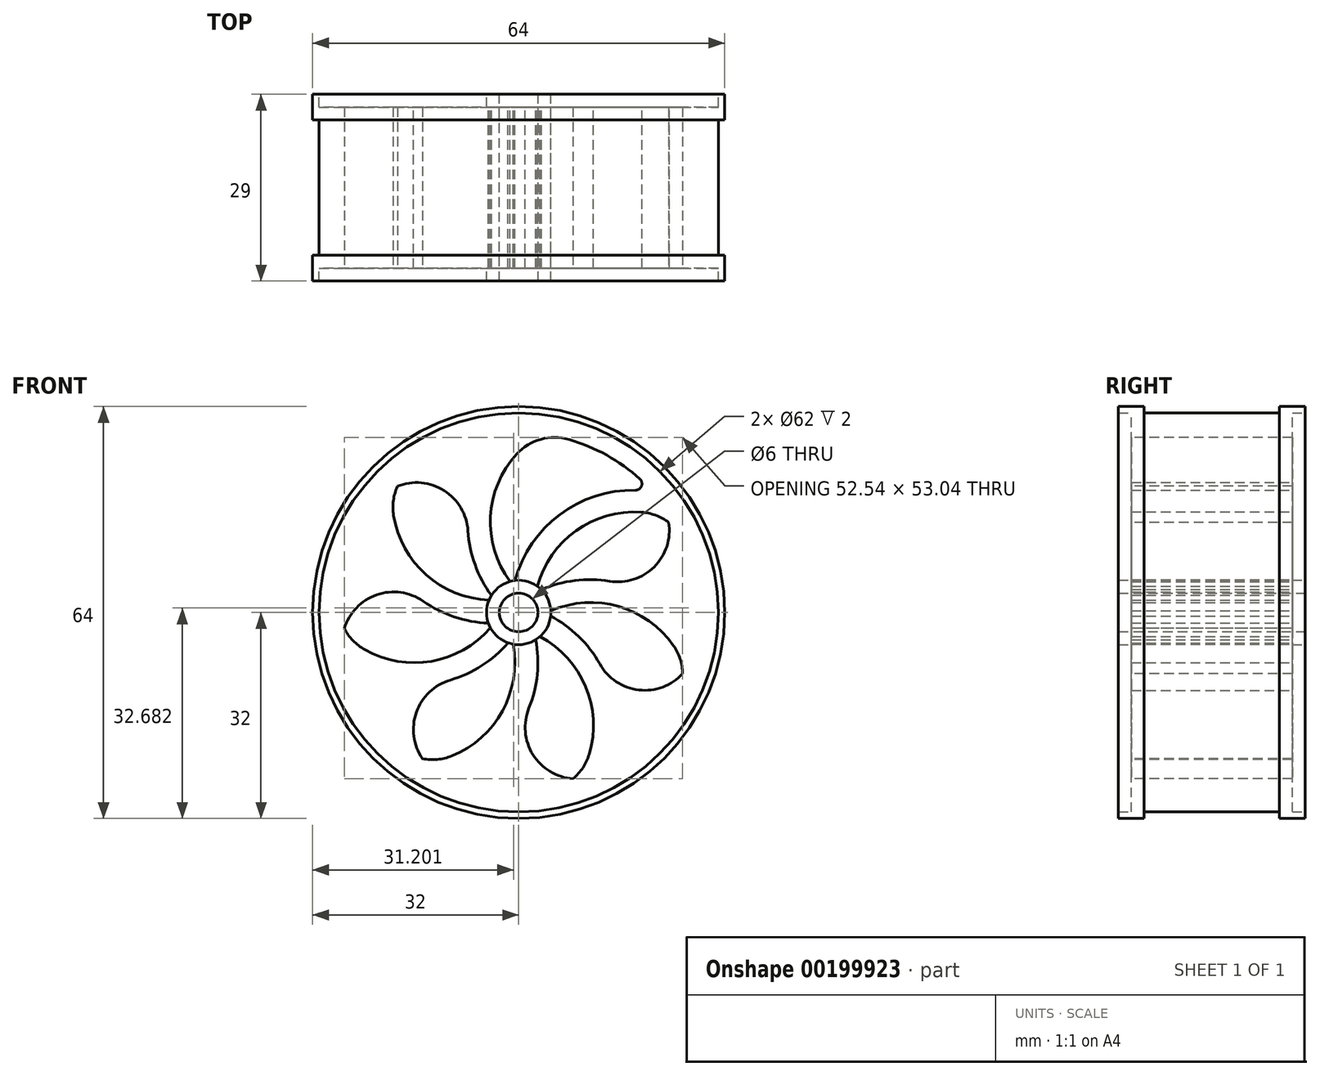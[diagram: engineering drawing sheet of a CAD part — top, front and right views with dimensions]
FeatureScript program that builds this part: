
annotation { "Feature Type Name" : "Feature", "Feature Type Description" : "" }
export const myFeature = defineFeature(function(context is Context, id is Id, definition is map)
    precondition{}
    {
        {
            var Q0;
            Q0=qCreatedBy(makeId("Front.planeOp"),FACE);
            var sketch = newSketch(context, id + "F0", { "sketchPlane" : qUnion([Q0])});
            skCircle(sketch, "E0", {"center": v(0, 0) * mm, "radius": 3 * mm});
            skCircle(sketch, "E1", {"center": v(0, 0) * mm, "radius": 5 * mm});
            skCircle(sketch, "E2", {"center": v(0, 0) * mm, "radius": 28 * mm});
            skCircle(sketch, "E3", {"center": v(0, 0) * mm, "radius": 31 * mm});
            skCircle(sketch, "E4", {"center": v(0, 0) * mm, "radius": 32 * mm});
            skArc(sketch, "E5", {"start": v(23.84, 14.68) * mm, "mid": v(11.32, 13.16) * mm, "end": v(4.15, 2.79) * mm, "construction": true});
            skArc(sketch, "E6", {"start": v(20.79, 18.76) * mm, "mid": v(7.46, 15.96) * mm, "end": v(-0.56, 4.97) * mm});
            skArc(sketch, "E7.trimOffspring", {"start": v(24, 14.41) * mm, "mid": v(11.11, 14.02) * mm, "end": v(2.92, 4.06) * mm});
            skPoint(sketch, "E8.center.orphan", {"position": v(20.77, 0) * mm});
            skSolve(sketch);
        }
        {
            var Q0;
            Q0=makeQuery(id+"F0.imprint","IMPRINT",FACE,{"disambiguationData":[TD([[makeQuery(id+"F0.imprint","IMPRINT",EDGE,{"derivedFrom":sQuery(id+"F0.wireOp",EDGE,"E3")}),1.0]])]});
            var Q1;
            {var subQ0=sQuery(id+"F0.wireOp",EDGE,"E6");Q1=makeQuery(id+"F0.imprint","IMPRINT",FACE,{"disambiguationData":[TD([[makeQuery(id+"F0.imprint","IMPRINT",EDGE,{"derivedFrom":subQ0}),1.0]])]});}
            var Q2;
            Q2=makeQuery(id+"F0.imprint","IMPRINT",FACE,{"disambiguationData":[TD([[makeQuery(id+"F0.imprint","IMPRINT",EDGE,{"derivedFrom":sQuery(id+"F0.wireOp",EDGE,"E0")}),-1.0]])]});
            extrude(context, id + "F1", {"entities" : qUnion([Q0, Q1, Q2]), "depth" : 25 * mm});
        }
        {
            var Q0;
            Q0=makeQuery(id+"F1.opExtrude","SWEPT_BODY",BODY,{"disambiguationData":[OSD([sQuery(id+"F0.wireOp",EDGE,"E0"),sQuery(id+"F0.wireOp",EDGE,"E1"),sQuery(id+"F0.wireOp",EDGE,"E2"),sQuery(id+"F0.wireOp",EDGE,"E3"),sQuery(id+"F0.wireOp",EDGE,"E6"),sQuery(id+"F0.wireOp",EDGE,"E7.trimOffspring")])]});
            var Q1;
            Q1=makeQuery(id+"F1.opExtrude","CAP_EDGE",EDGE,{"disambiguationData":[OSD([sQuery(id+"F0.wireOp",EDGE,"E0")])],"isStart":true});
            circularPattern(context, id + "F2", {"entities" : qUnion([Q0]), "axis" : qUnion([Q1]), "angle" : 360 * degree, "instanceCount" : 7, "equalSpace" : true});
        }
        {
            var Q0;
            Q0=makeQuery(id+"F0.imprint","IMPRINT",FACE,{"disambiguationData":[TD([[makeQuery(id+"F0.imprint","IMPRINT",EDGE,{"derivedFrom":sQuery(id+"F0.wireOp",EDGE,"E0")}),-1.0]])]});
            extrude(context, id + "F3", {"entities" : qUnion([Q0]), "operationType" : NewBodyOperationType.ADD, "depth" : 27 * mm});
        }
        {
            var Q0;
            Q0=makeQuery(id+"F0.imprint","IMPRINT",FACE,{"disambiguationData":[TD([[makeQuery(id+"F0.imprint","IMPRINT",EDGE,{"derivedFrom":sQuery(id+"F0.wireOp",EDGE,"E0")}),-1.0]])]});
            extrude(context, id + "F4", {"entities" : qUnion([Q0]), "operationType" : NewBodyOperationType.ADD, "oppositeDirection" : true, "depth" : 2 * mm});
        }
        {
            var Q0;
            Q0=makeQuery(id+"F0.imprint","IMPRINT",FACE,{"disambiguationData":[TD([[makeQuery(id+"F0.imprint","IMPRINT",EDGE,{"derivedFrom":sQuery(id+"F0.wireOp",EDGE,"E3")}),-1.0]])]});
            extrude(context, id + "F5", {"entities" : qUnion([Q0]), "operationType" : NewBodyOperationType.ADD, "depth" : 27 * mm});
        }
        {
            var Q0;
            Q0=makeQuery(id+"F0.imprint","IMPRINT",FACE,{"disambiguationData":[TD([[makeQuery(id+"F0.imprint","IMPRINT",EDGE,{"derivedFrom":sQuery(id+"F0.wireOp",EDGE,"E3")}),-1.0]])]});
            extrude(context, id + "F6", {"entities" : qUnion([Q0]), "operationType" : NewBodyOperationType.REMOVE, "depth" : 23 * mm});
        }
        {
            var Q0;
            Q0=makeQuery(id+"F0.imprint","IMPRINT",FACE,{"disambiguationData":[TD([[makeQuery(id+"F0.imprint","IMPRINT",EDGE,{"derivedFrom":sQuery(id+"F0.wireOp",EDGE,"E3")}),-1.0]])]});
            extrude(context, id + "F7", {"entities" : qUnion([Q0]), "operationType" : NewBodyOperationType.ADD, "endBound" : BoundingType.SYMMETRIC, "depth" : 4 * mm});
        }
        {
            var Q0;
            {var subQ0=makeQuery(id+"F1.opExtrude","SWEPT_FACE",FACE,{"disambiguationData":[OSD([sQuery(id+"F0.wireOp",EDGE,"E2")])]});Q0=makeQuery(id+"F3.boolean.opBoolean","INTERSECT",EDGE,{"disambiguationData":[OD(1.0)],"derivedFrom":[subQ0,makeQuery(id+"F2.opPattern","COPY",FACE,{"derivedFrom":subQ0,"instanceName":"1"}),makeQuery(id+"F2.opPattern","COPY",FACE,{"derivedFrom":subQ0,"instanceName":"2"}),makeQuery(id+"F2.opPattern","COPY",FACE,{"derivedFrom":subQ0,"instanceName":"4"})]});}
            var Q1;
            {var subQ0=makeQuery(id+"F1.opExtrude","SWEPT_FACE",FACE,{"disambiguationData":[OSD([sQuery(id+"F0.wireOp",EDGE,"E2")])]});Q1=makeQuery(id+"F3.boolean.opBoolean","INTERSECT",EDGE,{"disambiguationData":[OD(1.0)],"derivedFrom":[subQ0,makeQuery(id+"F2.opPattern","COPY",FACE,{"derivedFrom":subQ0,"instanceName":"1"}),makeQuery(id+"F2.opPattern","COPY",FACE,{"derivedFrom":subQ0,"instanceName":"2"}),makeQuery(id+"F2.opPattern","COPY",FACE,{"derivedFrom":subQ0,"instanceName":"3"}),makeQuery(id+"F2.opPattern","COPY",FACE,{"derivedFrom":subQ0,"instanceName":"5"})]});}
            var Q2;
            {var subQ0=makeQuery(id+"F1.opExtrude","SWEPT_FACE",FACE,{"disambiguationData":[OSD([sQuery(id+"F0.wireOp",EDGE,"E2")])]});Q2=makeQuery(id+"F3.boolean.opBoolean","INTERSECT",EDGE,{"disambiguationData":[OD(1.0)],"derivedFrom":[subQ0,makeQuery(id+"F2.opPattern","COPY",FACE,{"derivedFrom":subQ0,"instanceName":"1"}),makeQuery(id+"F2.opPattern","COPY",FACE,{"derivedFrom":subQ0,"instanceName":"2"}),makeQuery(id+"F2.opPattern","COPY",FACE,{"derivedFrom":subQ0,"instanceName":"3"}),makeQuery(id+"F2.opPattern","COPY",FACE,{"derivedFrom":subQ0,"instanceName":"4"}),makeQuery(id+"F2.opPattern","COPY",FACE,{"derivedFrom":subQ0,"instanceName":"6"})]});}
            var Q3;
            {var subQ0=makeQuery(id+"F1.opExtrude","SWEPT_FACE",FACE,{"disambiguationData":[OSD([sQuery(id+"F0.wireOp",EDGE,"E2")])]});Q3=makeQuery(id+"F3.boolean.opBoolean","INTERSECT",EDGE,{"disambiguationData":[OD(1.0)],"derivedFrom":[subQ0,makeQuery(id+"F2.opPattern","COPY",FACE,{"derivedFrom":subQ0,"instanceName":"1"}),makeQuery(id+"F2.opPattern","COPY",FACE,{"derivedFrom":subQ0,"instanceName":"2"}),makeQuery(id+"F2.opPattern","COPY",FACE,{"derivedFrom":subQ0,"instanceName":"3"}),makeQuery(id+"F2.opPattern","COPY",FACE,{"derivedFrom":subQ0,"instanceName":"4"}),makeQuery(id+"F2.opPattern","COPY",FACE,{"derivedFrom":subQ0,"instanceName":"5"})]});}
            var Q4;
            Q4=makeQuery(id+"F1.opExtrude","SWEPT_EDGE",EDGE,{"disambiguationData":[OSD([sQuery(id+"F0.wireOp",EDGE,"E2"),sQuery(id+"F0.wireOp",EDGE,"E7.trimOffspring")])]});
            var Q5;
            {var subQ0=makeQuery(id+"F1.opExtrude","SWEPT_FACE",FACE,{"disambiguationData":[OSD([sQuery(id+"F0.wireOp",EDGE,"E2")])]});Q5=makeQuery(id+"F3.boolean.opBoolean","INTERSECT",EDGE,{"disambiguationData":[OD(1.0)],"derivedFrom":[subQ0,makeQuery(id+"F2.opPattern","COPY",FACE,{"derivedFrom":subQ0,"instanceName":"2"})]});}
            var Q6;
            {var subQ0=makeQuery(id+"F1.opExtrude","SWEPT_FACE",FACE,{"disambiguationData":[OSD([sQuery(id+"F0.wireOp",EDGE,"E2")])]});Q6=makeQuery(id+"F3.boolean.opBoolean","INTERSECT",EDGE,{"disambiguationData":[OD(1.0)],"derivedFrom":[subQ0,makeQuery(id+"F2.opPattern","COPY",FACE,{"derivedFrom":subQ0,"instanceName":"1"}),makeQuery(id+"F2.opPattern","COPY",FACE,{"derivedFrom":subQ0,"instanceName":"3"})]});}
            fillet(context, id + "F8", {"entities" : qUnion([Q0, Q1, Q2, Q3, Q4, Q5, Q6]), "radius" : 8 * mm, "tangentPropagation" : true, "allowEdgeOverflow" : false});
        }
        {
            var Q0;
            {var subQ0=makeQuery(id+"F1.opExtrude","SWEPT_FACE",FACE,{"disambiguationData":[OSD([sQuery(id+"F0.wireOp",EDGE,"E2")])]});Q0=makeQuery(id+"F3.boolean.opBoolean","INTERSECT",EDGE,{"disambiguationData":[OD(0.0)],"derivedFrom":[subQ0,makeQuery(id+"F2.opPattern","COPY",FACE,{"derivedFrom":subQ0,"instanceName":"1"}),makeQuery(id+"F2.opPattern","COPY",FACE,{"derivedFrom":subQ0,"instanceName":"3"})]});}
            var Q1;
            {var subQ0=makeQuery(id+"F1.opExtrude","SWEPT_FACE",FACE,{"disambiguationData":[OSD([sQuery(id+"F0.wireOp",EDGE,"E2")])]});Q1=makeQuery(id+"F3.boolean.opBoolean","INTERSECT",EDGE,{"disambiguationData":[OD(0.0)],"derivedFrom":[subQ0,makeQuery(id+"F2.opPattern","COPY",FACE,{"derivedFrom":subQ0,"instanceName":"2"})]});}
            var Q2;
            Q2=makeQuery(id+"F1.opExtrude","SWEPT_EDGE",EDGE,{"disambiguationData":[OSD([sQuery(id+"F0.wireOp",EDGE,"E2"),sQuery(id+"F0.wireOp",EDGE,"E6")])]});
            var Q3;
            {var subQ0=makeQuery(id+"F1.opExtrude","SWEPT_FACE",FACE,{"disambiguationData":[OSD([sQuery(id+"F0.wireOp",EDGE,"E2")])]});Q3=makeQuery(id+"F3.boolean.opBoolean","INTERSECT",EDGE,{"disambiguationData":[OD(0.0)],"derivedFrom":[subQ0,makeQuery(id+"F2.opPattern","COPY",FACE,{"derivedFrom":subQ0,"instanceName":"1"}),makeQuery(id+"F2.opPattern","COPY",FACE,{"derivedFrom":subQ0,"instanceName":"2"}),makeQuery(id+"F2.opPattern","COPY",FACE,{"derivedFrom":subQ0,"instanceName":"3"}),makeQuery(id+"F2.opPattern","COPY",FACE,{"derivedFrom":subQ0,"instanceName":"4"}),makeQuery(id+"F2.opPattern","COPY",FACE,{"derivedFrom":subQ0,"instanceName":"5"})]});}
            var Q4;
            {var subQ0=makeQuery(id+"F1.opExtrude","SWEPT_FACE",FACE,{"disambiguationData":[OSD([sQuery(id+"F0.wireOp",EDGE,"E2")])]});Q4=makeQuery(id+"F3.boolean.opBoolean","INTERSECT",EDGE,{"disambiguationData":[OD(0.0)],"derivedFrom":[subQ0,makeQuery(id+"F2.opPattern","COPY",FACE,{"derivedFrom":subQ0,"instanceName":"1"}),makeQuery(id+"F2.opPattern","COPY",FACE,{"derivedFrom":subQ0,"instanceName":"2"}),makeQuery(id+"F2.opPattern","COPY",FACE,{"derivedFrom":subQ0,"instanceName":"3"}),makeQuery(id+"F2.opPattern","COPY",FACE,{"derivedFrom":subQ0,"instanceName":"4"}),makeQuery(id+"F2.opPattern","COPY",FACE,{"derivedFrom":subQ0,"instanceName":"6"})]});}
            var Q5;
            {var subQ0=makeQuery(id+"F1.opExtrude","SWEPT_FACE",FACE,{"disambiguationData":[OSD([sQuery(id+"F0.wireOp",EDGE,"E2")])]});Q5=makeQuery(id+"F3.boolean.opBoolean","INTERSECT",EDGE,{"disambiguationData":[OD(0.0)],"derivedFrom":[subQ0,makeQuery(id+"F2.opPattern","COPY",FACE,{"derivedFrom":subQ0,"instanceName":"1"}),makeQuery(id+"F2.opPattern","COPY",FACE,{"derivedFrom":subQ0,"instanceName":"2"}),makeQuery(id+"F2.opPattern","COPY",FACE,{"derivedFrom":subQ0,"instanceName":"3"}),makeQuery(id+"F2.opPattern","COPY",FACE,{"derivedFrom":subQ0,"instanceName":"5"})]});}
            var Q6;
            {var subQ0=makeQuery(id+"F1.opExtrude","SWEPT_FACE",FACE,{"disambiguationData":[OSD([sQuery(id+"F0.wireOp",EDGE,"E2")])]});Q6=makeQuery(id+"F3.boolean.opBoolean","INTERSECT",EDGE,{"disambiguationData":[OD(0.0)],"derivedFrom":[subQ0,makeQuery(id+"F2.opPattern","COPY",FACE,{"derivedFrom":subQ0,"instanceName":"1"}),makeQuery(id+"F2.opPattern","COPY",FACE,{"derivedFrom":subQ0,"instanceName":"2"}),makeQuery(id+"F2.opPattern","COPY",FACE,{"derivedFrom":subQ0,"instanceName":"4"})]});}
            fillet(context, id + "F9", {"entities" : qUnion([Q0, Q1, Q2, Q3, Q4, Q5, Q6]), "radius" : 1 * mm, "tangentPropagation" : true, "allowEdgeOverflow" : false});
        }
    });
